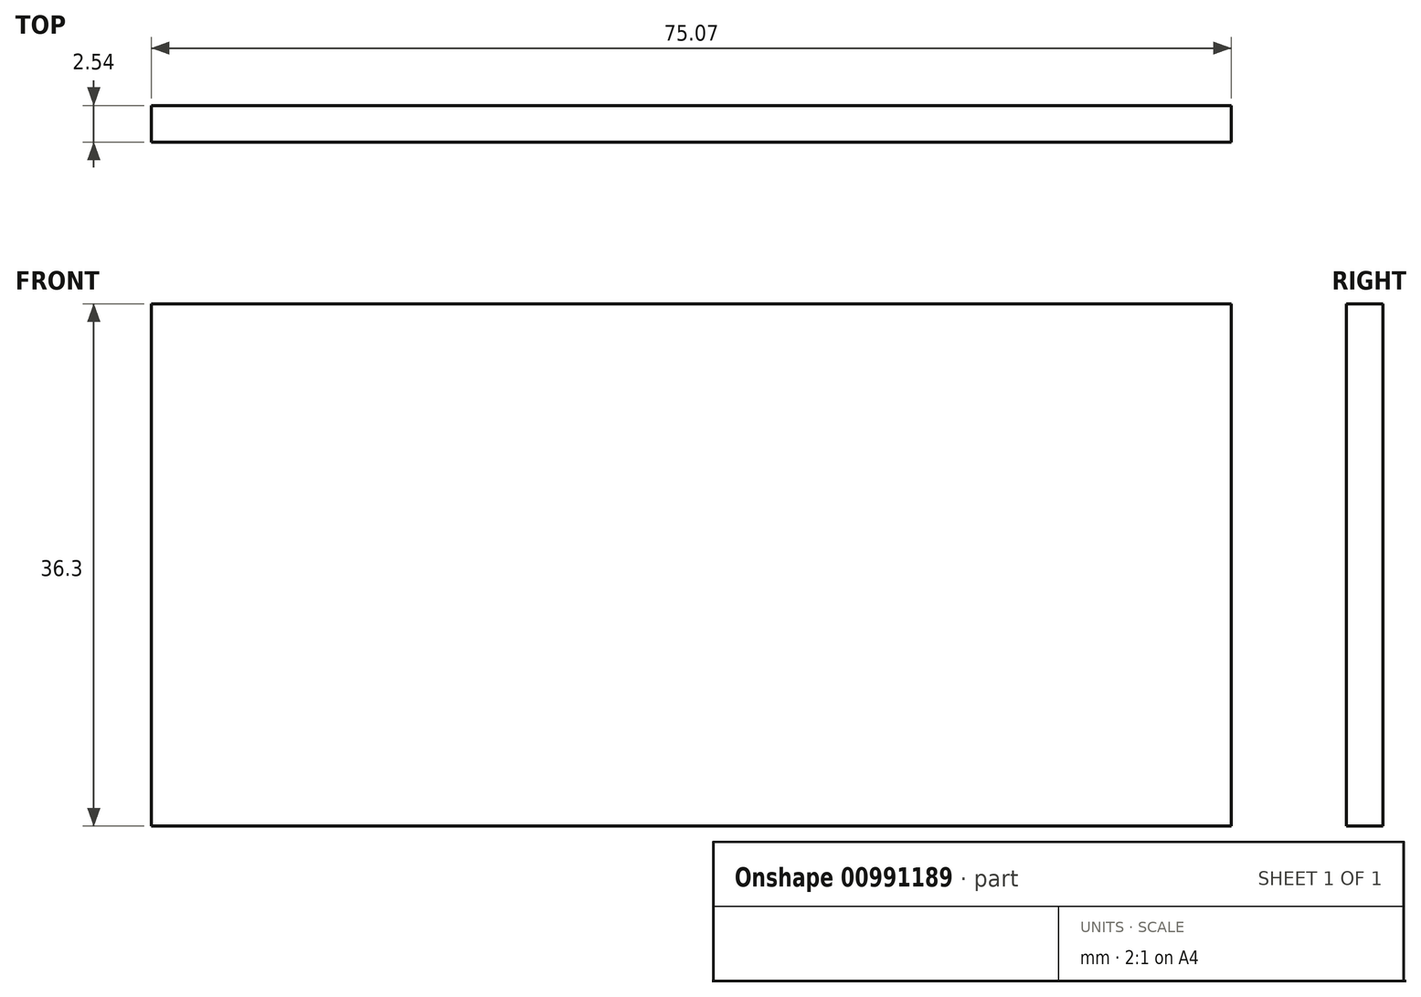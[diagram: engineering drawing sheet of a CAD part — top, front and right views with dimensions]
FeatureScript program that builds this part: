
annotation { "Feature Type Name" : "Feature", "Feature Type Description" : "" }
export const myFeature = defineFeature(function(context is Context, id is Id, definition is map)
    precondition{}
    {
        {
            var Q0;
            Q0=qCreatedBy(makeId("Front.planeOp"),FACE);
            var sketch = newSketch(context, id + "F0", { "sketchPlane" : qUnion([Q0])});
            skLineSegment(sketch, "E0.bottom", {"start": v(-51.72, 24.23) * mm, "end": v(23.35, 24.23) * mm});
            skLineSegment(sketch, "E0.top", {"start": v(-51.72, -12.07) * mm, "end": v(23.35, -12.07) * mm});
            skLineSegment(sketch, "E0.left", {"start": v(-51.72, 24.23) * mm, "end": v(-51.72, -12.07) * mm});
            skLineSegment(sketch, "E0.right", {"start": v(23.35, 24.23) * mm, "end": v(23.35, -12.07) * mm});
            skSolve(sketch);
        }
        {
            var Q0;
            Q0=makeQuery(id+"F0.imprint","IMPRINT",FACE,{"disambiguationData":[TD([[makeQuery(id+"F0.imprint","IMPRINT",EDGE,{"derivedFrom":sQuery(id+"F0.wireOp",EDGE,"E0.bottom")}),-1.0]])]});
            extrude(context, id + "F1", {"entities" : qUnion([Q0]), "depth" : 2.54 * mm, "offsetDistance" : 25.4 * mm});
        }
    });
